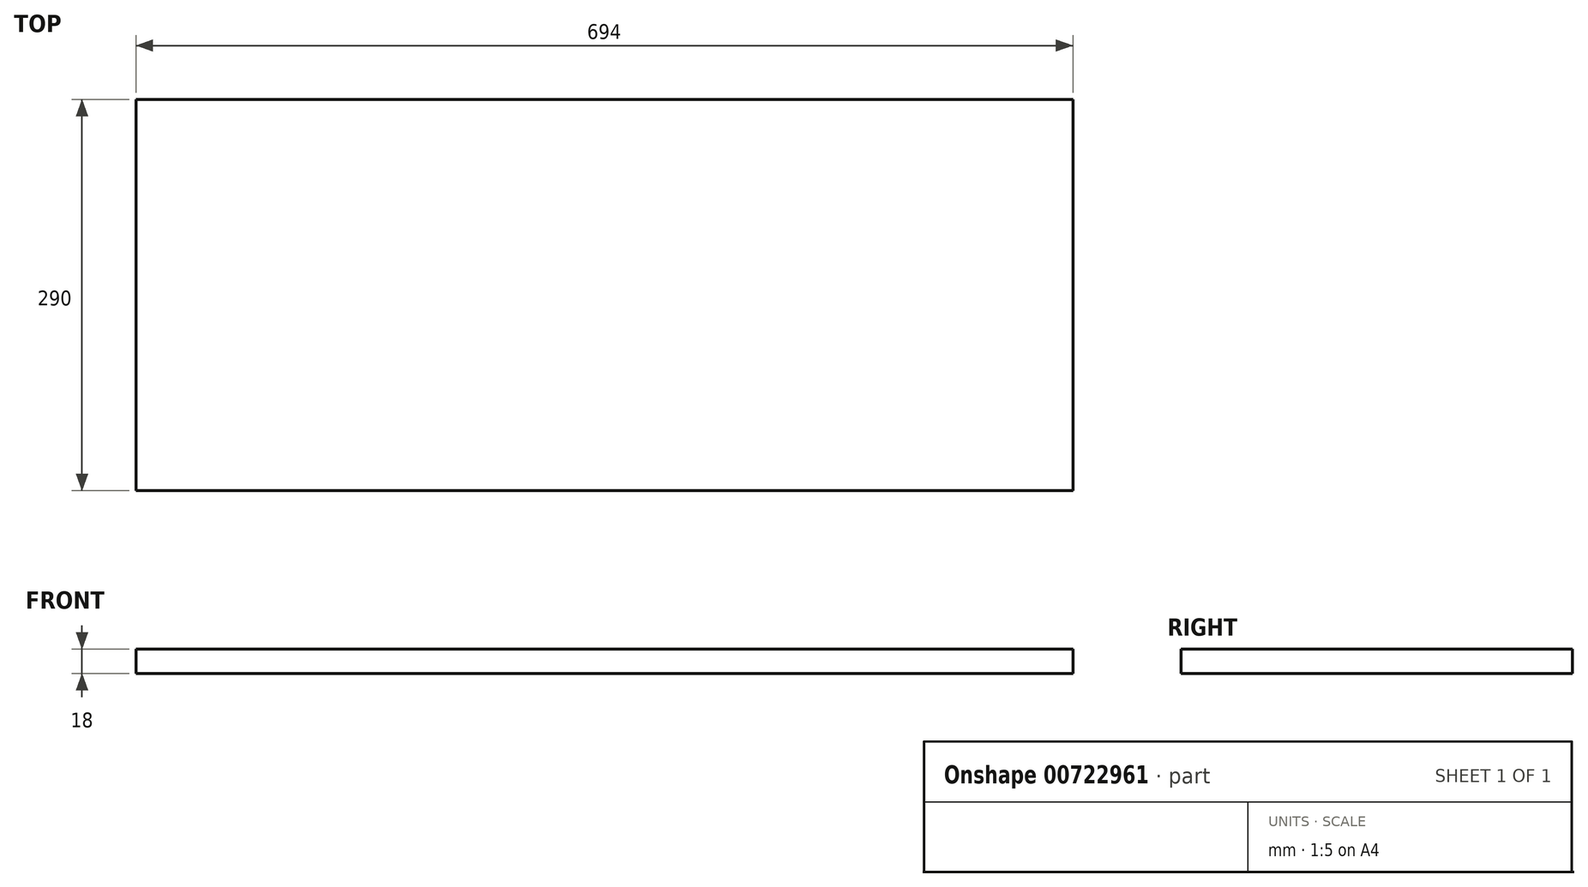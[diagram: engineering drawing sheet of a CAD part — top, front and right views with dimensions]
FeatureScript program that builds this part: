
annotation { "Feature Type Name" : "Feature", "Feature Type Description" : "" }
export const myFeature = defineFeature(function(context is Context, id is Id, definition is map)
    precondition{}
    {
        {
            var Q0;
            Q0=qCreatedBy(makeId("Top.planeOp"),FACE);
            var sketch = newSketch(context, id + "F0", { "sketchPlane" : qUnion([Q0])});
            skLineSegment(sketch, "E0.bottom", {"start": v(-347, 145) * mm, "end": v(347, 145) * mm});
            skLineSegment(sketch, "E0.top", {"start": v(-347, -145) * mm, "end": v(347, -145) * mm});
            skLineSegment(sketch, "E0.left", {"start": v(-347, 145) * mm, "end": v(-347, -145) * mm});
            skLineSegment(sketch, "E0.right", {"start": v(347, 145) * mm, "end": v(347, -145) * mm});
            skLineSegment(sketch, "E1", {"start": v(-347, 145) * mm, "end": v(347, -145) * mm, "construction": true});
            skLineSegment(sketch, "E2", {"start": v(347, 145) * mm, "end": v(-347, -145) * mm, "construction": true});
            skSolve(sketch);
        }
        {
            var Q0;
            Q0 = qSketchRegion(id + "F0", true);
            extrude(context, id + "F1", {"entities" : qUnion([Q0]), "depth" : 18 * mm, "offsetDistance" : 25 * mm});
        }
    });
